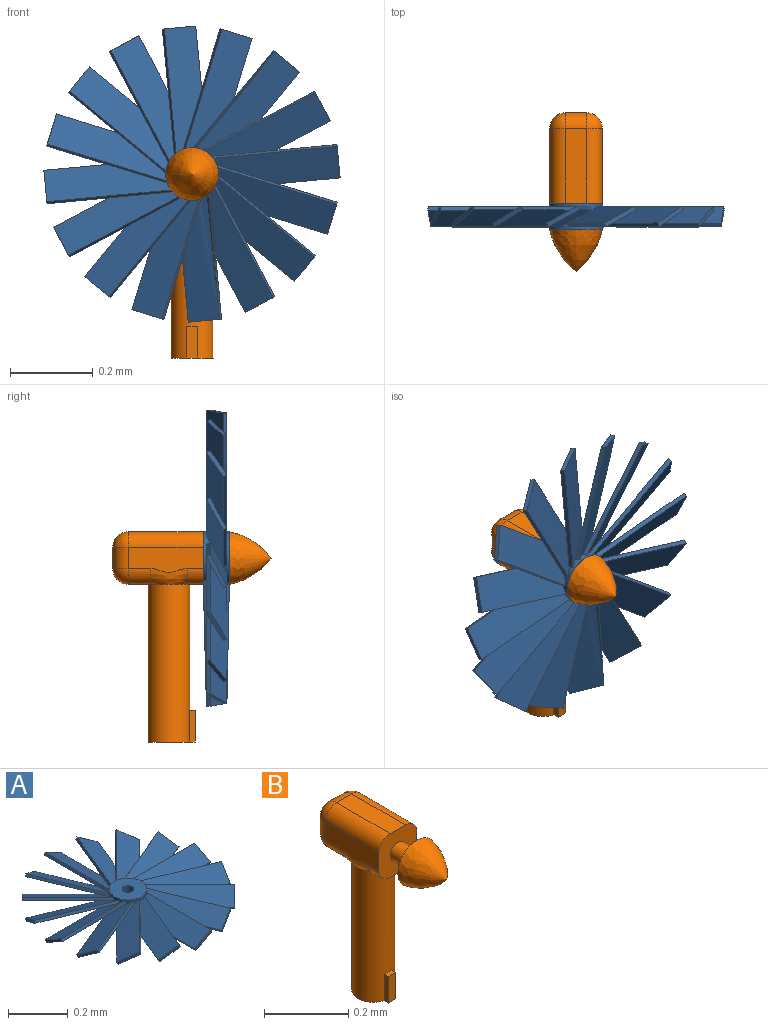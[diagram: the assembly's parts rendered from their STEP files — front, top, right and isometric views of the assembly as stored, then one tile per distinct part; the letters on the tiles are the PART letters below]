
ASSEMBLY  parts=2 mates=1
PART A: 85 faces, bbox 0.7x0.7x0.1 mm
  f0: cylinder r=0.06mm len=0.13mm, axis (0,0,-1), area 0mm2, adj f3,f8,f9,f13,f14,f18,f19,f23
  f1: cylinder r=0.02mm len=0.06mm, axis (0,0,-1), area 0mm2, adj f3,f4
  f2: cylinder r=0.06mm len=0.13mm, axis (0,0,-1), area 0mm2, adj f4,f5,f6,f8,f10,f11,f15,f16
  f3: plane 0.13x0.13mm, normal (0,0,1), area 0mm2, adj f0,f1
  f4: plane 0.13x0.13mm, normal (0,0,-1), area 0mm2, adj f1,f2
  f5: plane 0.31x0.02mm, normal (0,0.88,-0.47), area 0mm2, adj f2,f6,f7,f8
  f6: plane 0.31x0.09mm, normal (0,-0.47,-0.88), area 0mm2, adj f2,f5,f7,f9,f13
  f7: plane 0.08x0.05mm, normal (-1,0,0), area 0mm2, adj f5,f6,f8,f9
  f8: plane 0.31x0.08mm, normal (0,0.47,0.88), area 0mm2, adj f0,f2,f5,f7,f9,f81,f84
  f9: plane 0.31x0.02mm, normal (0,-0.88,0.47), area 0mm2, adj f0,f6,f7,f8
  f10: plane 0.28x0.12mm, normal (-0.34,0.82,-0.47), area 0mm2, adj f2,f11,f12,f13
  f11: plane 0.32x0.19mm, normal (0.18,-0.43,-0.88), area 0mm2, adj f2,f10,f12,f14,f18
  f12: plane 0.08x0.05mm, normal (-0.92,-0.38,0), area 0mm2, adj f10,f11,f13,f14
  f13: plane 0.31x0.19mm, normal (-0.18,0.43,0.88), area 0mm2, adj f0,f6,f10,f12,f14
  f14: plane 0.29x0.12mm, normal (0.34,-0.82,0.47), area 0mm2, adj f0,f11,f12,f13,f18
  f15: plane 0.22x0.22mm, normal (-0.62,0.62,-0.47), area 0mm2, adj f2,f16,f17,f18
  f16: plane 0.27x0.27mm, normal (0.33,-0.33,-0.88), area 0mm2, adj f2,f15,f17,f19,f23
  f17: plane 0.06x0.06mm, normal (-0.71,-0.71,0), area 0mm2, adj f15,f16,f18,f19
  f18: plane 0.27x0.27mm, normal (-0.33,0.33,0.88), area 0mm2, adj f0,f2,f11,f14,f15,f17,f19
  f19: plane 0.22x0.22mm, normal (0.62,-0.62,0.47), area 0mm2, adj f0,f16,f17,f18,f23
  f20: plane 0.28x0.12mm, normal (-0.82,0.34,-0.47), area 0mm2, adj f2,f21,f22,f23
  f21: plane 0.31x0.19mm, normal (0.43,-0.18,-0.88), area 0mm2, adj f2,f20,f22,f24,f28
  f22: plane 0.08x0.05mm, normal (-0.38,-0.92,0), area 0mm2, adj f20,f21,f23,f24
  f23: plane 0.31x0.19mm, normal (-0.43,0.18,0.88), area 0mm2, adj f0,f2,f16,f19,f20,f22,f24
  f24: plane 0.29x0.12mm, normal (0.82,-0.34,0.47), area 0mm2, adj f0,f21,f22,f23,f28
  f25: plane 0.31x0.01mm, normal (-0.88,0,-0.47), area 0mm2, adj f2,f26,f27,f28
  f26: plane 0.31x0.08mm, normal (0.47,0,-0.88), area 0mm2, adj f2,f25,f27,f29,f33
  f27: plane 0.08x0.05mm, normal (0,-1,0), area 0mm2, adj f25,f26,f28,f29
  f28: plane 0.31x0.08mm, normal (-0.47,0,0.88), area 0mm2, adj f0,f2,f21,f24,f25,f27,f29
  f29: plane 0.31x0.01mm, normal (0.88,0,0.47), area 0mm2, adj f0,f26,f27,f28,f33
  f30: plane 0.28x0.12mm, normal (-0.82,-0.34,-0.47), area 0mm2, adj f2,f31,f32,f33
  f31: plane 0.32x0.19mm, normal (0.43,0.18,-0.88), area 0mm2, adj f2,f30,f32,f34,f38
  f32: plane 0.08x0.05mm, normal (0.38,-0.92,0), area 0mm2, adj f30,f31,f33,f34
  f33: plane 0.31x0.19mm, normal (-0.43,-0.18,0.88), area 0mm2, adj f0,f2,f26,f29,f30,f32,f34
  f34: plane 0.29x0.12mm, normal (0.82,0.34,0.47), area 0mm2, adj f0,f31,f32,f33,f38
  f35: plane 0.22x0.22mm, normal (-0.62,-0.62,-0.47), area 0mm2, adj f2,f36,f37,f38
  f36: plane 0.27x0.27mm, normal (0.33,0.33,-0.88), area 0mm2, adj f2,f35,f37,f39,f43
  f37: plane 0.06x0.06mm, normal (0.71,-0.71,0), area 0mm2, adj f35,f36,f38,f39
  f38: plane 0.27x0.27mm, normal (-0.33,-0.33,0.88), area 0mm2, adj f0,f2,f31,f34,f35,f37,f39
  f39: plane 0.22x0.22mm, normal (0.62,0.62,0.47), area 0mm2, adj f0,f36,f37,f38,f43
  f40: plane 0.28x0.12mm, normal (-0.34,-0.82,-0.47), area 0mm2, adj f2,f41,f42,f43
  f41: plane 0.31x0.19mm, normal (0.18,0.43,-0.88), area 0mm2, adj f2,f40,f42,f44,f48
  f42: plane 0.08x0.05mm, normal (0.92,-0.38,0), area 0mm2, adj f40,f41,f43,f44
  f43: plane 0.31x0.19mm, normal (-0.18,-0.43,0.88), area 0mm2, adj f0,f2,f36,f39,f40,f42,f44
  f44: plane 0.29x0.12mm, normal (0.34,0.82,0.47), area 0mm2, adj f0,f41,f42,f43,f48
  f45: plane 0.31x0.01mm, normal (0,-0.88,-0.47), area 0mm2, adj f2,f46,f47,f48
  f46: plane 0.31x0.08mm, normal (0,0.47,-0.88), area 0mm2, adj f2,f45,f47,f49,f53
  f47: plane 0.08x0.05mm, normal (1,0,0), area 0mm2, adj f45,f46,f48,f49
  f48: plane 0.31x0.08mm, normal (0,-0.47,0.88), area 0mm2, adj f0,f2,f41,f44,f45,f47,f49
  f49: plane 0.31x0.01mm, normal (0,0.88,0.47), area 0mm2, adj f0,f46,f47,f48,f53
  f50: plane 0.28x0.12mm, normal (0.34,-0.82,-0.47), area 0mm2, adj f2,f51,f52,f53
  f51: plane 0.32x0.19mm, normal (-0.18,0.43,-0.88), area 0mm2, adj f2,f50,f52,f54,f58
  f52: plane 0.08x0.05mm, normal (0.92,0.38,0), area 0mm2, adj f50,f51,f53,f54
  f53: plane 0.31x0.19mm, normal (0.18,-0.43,0.88), area 0mm2, adj f0,f2,f46,f49,f50,f52,f54
  f54: plane 0.29x0.12mm, normal (-0.34,0.82,0.47), area 0mm2, adj f0,f51,f52,f53,f58
  f55: plane 0.22x0.22mm, normal (0.62,-0.62,-0.47), area 0mm2, adj f2,f56,f57,f58
  f56: plane 0.27x0.27mm, normal (-0.33,0.33,-0.88), area 0mm2, adj f2,f55,f57,f59,f63
  f57: plane 0.06x0.06mm, normal (0.71,0.71,0), area 0mm2, adj f55,f56,f58,f59
  f58: plane 0.27x0.27mm, normal (0.33,-0.33,0.88), area 0mm2, adj f0,f2,f51,f54,f55,f57,f59
  f59: plane 0.22x0.22mm, normal (-0.62,0.62,0.47), area 0mm2, adj f0,f56,f57,f58,f63
  f60: plane 0.28x0.12mm, normal (0.82,-0.34,-0.47), area 0mm2, adj f2,f61,f62,f63
  f61: plane 0.31x0.19mm, normal (-0.43,0.18,-0.88), area 0mm2, adj f2,f60,f62,f64,f68
  f62: plane 0.08x0.05mm, normal (0.38,0.92,0), area 0mm2, adj f60,f61,f63,f64
  f63: plane 0.31x0.19mm, normal (0.43,-0.18,0.88), area 0mm2, adj f0,f2,f56,f59,f60,f62,f64
  f64: plane 0.29x0.12mm, normal (-0.82,0.34,0.47), area 0mm2, adj f0,f61,f62,f63,f68
  f65: plane 0.31x0.01mm, normal (0.88,0,-0.47), area 0mm2, adj f2,f66,f67,f68
  f66: plane 0.31x0.08mm, normal (-0.47,0,-0.88), area 0mm2, adj f2,f65,f67,f69,f73
  f67: plane 0.08x0.05mm, normal (0,1,0), area 0mm2, adj f65,f66,f68,f69
  f68: plane 0.31x0.08mm, normal (0.47,0,0.88), area 0mm2, adj f0,f2,f61,f64,f65,f67,f69
  f69: plane 0.31x0.01mm, normal (-0.88,0,0.47), area 0mm2, adj f0,f66,f67,f68,f73
  f70: plane 0.28x0.12mm, normal (0.82,0.34,-0.47), area 0mm2, adj f2,f71,f72,f73
  f71: plane 0.32x0.19mm, normal (-0.43,-0.18,-0.88), area 0mm2, adj f2,f70,f72,f74,f78
  f72: plane 0.08x0.05mm, normal (-0.38,0.92,0), area 0mm2, adj f70,f71,f73,f74
  f73: plane 0.31x0.19mm, normal (0.43,0.18,0.88), area 0mm2, adj f0,f2,f66,f69,f70,f72,f74
  f74: plane 0.29x0.12mm, normal (-0.82,-0.34,0.47), area 0mm2, adj f0,f71,f72,f73,f78
  f75: plane 0.22x0.22mm, normal (0.62,0.62,-0.47), area 0mm2, adj f2,f76,f77,f78
  f76: plane 0.27x0.27mm, normal (-0.33,-0.33,-0.88), area 0mm2, adj f2,f75,f77,f79,f83
  f77: plane 0.06x0.06mm, normal (-0.71,0.71,0), area 0mm2, adj f75,f76,f78,f79
  f78: plane 0.27x0.27mm, normal (0.33,0.33,0.88), area 0mm2, adj f0,f2,f71,f74,f75,f77,f79
  f79: plane 0.22x0.22mm, normal (-0.62,-0.62,0.47), area 0mm2, adj f0,f76,f77,f78,f83
  f80: plane 0.28x0.12mm, normal (0.34,0.82,-0.47), area 0mm2, adj f2,f81,f82,f83
  f81: plane 0.31x0.19mm, normal (-0.18,-0.43,-0.88), area 0mm2, adj f2,f8,f80,f82,f84
  f82: plane 0.08x0.05mm, normal (-0.92,0.38,0), area 0mm2, adj f80,f81,f83,f84
  f83: plane 0.31x0.19mm, normal (0.18,0.43,0.88), area 0mm2, adj f0,f2,f76,f79,f80,f82,f84
  f84: plane 0.29x0.12mm, normal (-0.34,-0.82,0.47), area 0mm2, adj f0,f8,f81,f82,f83
PART B: 32 faces, bbox 0.1x0.4x0.5 mm
  f0: plane 0.05x0.04mm, normal (0,0,-1), area 0mm2, adj f1,f5,f8,f11
  f1: cylinder r=0.05mm len=0.38mm, axis (0,0,-1), area 0.1mm2, adj f0,f7,f9,f12,f27,f28,f30,f31
  f2: plane 0.18x0.06mm, normal (1,0,0), area 0mm2, adj f5,f11,f12,f13,f15,f18
  f3: plane 0.05x0.05mm, normal (0,1,0), area 0mm2, adj f18,f19,f22,f23
  f4: plane 0.18x0.06mm, normal (-1,0,0), area 0mm2, adj f5,f8,f9,f10,f14,f23
  f5: plane 0.13x0.13mm, normal (0,-1,0), area 0mm2, adj f0,f2,f4,f6,f8,f11,f14,f15
  f6: plane 0.18x0.05mm, normal (0,0,1), area 0mm2, adj f5,f14,f15,f19
  f7: plane 0.05x0.05mm, normal (0,0,-1), area 0mm2, adj f1,f10,f13,f22
  f8: cylinder r=0.04mm len=0.04mm, axis (0,-1,0), area 0mm2, adj f0,f4,f5,f9
  f9: bspline ~0.09x0.04mm, area 0mm2, adj f1,f4,f8,f10
  f10: cylinder r=0.04mm len=0.05mm, axis (0,-1,0), area 0mm2, adj f4,f7,f9,f24
  f11: cylinder r=0.04mm len=0.04mm, axis (0,1,0), area 0mm2, adj f0,f2,f5,f12
  f12: bspline ~0.09x0.04mm, area 0mm2, adj f1,f2,f11,f13
  f13: cylinder r=0.04mm len=0.05mm, axis (0,1,0), area 0mm2, adj f2,f7,f12,f20
  f14: cylinder r=0.04mm len=0.18mm, axis (0,1,0), area 0mm2, adj f4,f5,f6,f21
  f15: cylinder r=0.04mm len=0.18mm, axis (0,-1,0), area 0mm2, adj f2,f5,f6,f17
  f16: cylinder r=0.03mm len=0.06mm, axis (0,1,0), area 0mm2, adj f5,f25
  f17: sphere r=0.04mm, area 0mm2, adj f15,f18,f19
  f18: cylinder r=0.04mm len=0.05mm, axis (0,0,1), area 0mm2, adj f2,f3,f17,f20
  f19: cylinder r=0.04mm len=0.05mm, axis (1,0,0), area 0mm2, adj f3,f6,f17,f21
  f20: sphere r=0.04mm, area 0mm2, adj f13,f18,f22
  f21: sphere r=0.04mm, area 0mm2, adj f14,f19,f23
  f22: cylinder r=0.04mm len=0.05mm, axis (-1,0,0), area 0mm2, adj f3,f7,f20,f24
  f23: cylinder r=0.04mm len=0.05mm, axis (0,0,-1), area 0mm2, adj f3,f4,f21,f24
  f24: sphere r=0.04mm, area 0mm2, adj f10,f22,f23
  f25: plane 0.13x0.13mm, normal (0,1,0), area 0mm2, adj f16,f26
  f26: revolved ~0.13x0.13mm, area 0mm2, adj f25
  f27: plane 0.08x0.01mm, normal (-1,0,0), area 0mm2, adj f1,f29,f30,f31
  f28: plane 0.08x0.01mm, normal (1,0,0), area 0mm2, adj f1,f29,f30,f31
  f29: plane 0.08x0.03mm, normal (0,-1,0), area 0mm2, adj f27,f28,f30,f31
  f30: plane 0.11x0.1mm, normal (0,0,-1), area 0mm2, adj f1,f27,f28,f29
  f31: plane 0.03x0.01mm, normal (0,0,1), area 0mm2, adj f1,f27,f28,f29
PLACE A rot(axis=(-0.54,-0.59,-0.59),123.2deg) t=(-0.36,-0.03,1.28)mm
PLACE B t=(-0.22,0.12,0.27)mm fixed
MATE revolute A.f0 <-> B.f16  axis (0,-1,0) through (-0.22,-0.03,0.72)mm
